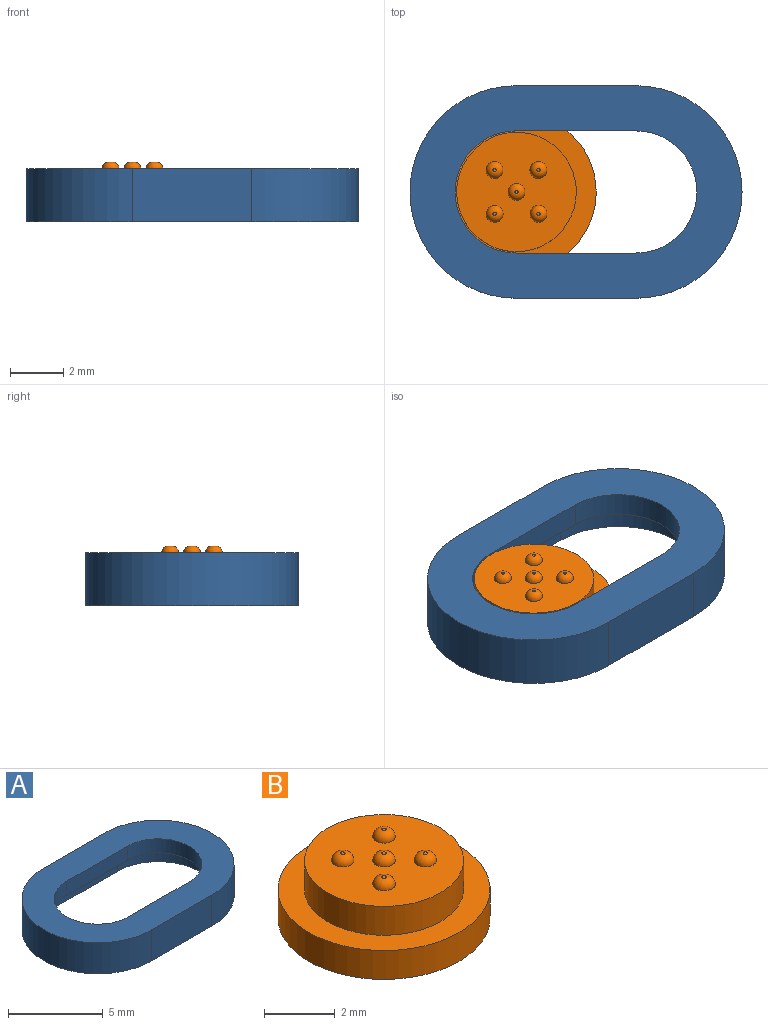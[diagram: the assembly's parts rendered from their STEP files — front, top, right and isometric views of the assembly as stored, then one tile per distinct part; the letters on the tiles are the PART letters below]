
ASSEMBLY  parts=2 mates=1
PART A: 15 faces, bbox 12.5x8x2 mm
  f0: plane 12.5x8mm, normal (0,0,-1), area 29.6mm2, adj f2,f3,f4,f5,f11,f12,f13,f14
  f1: plane 12.5x8mm, normal (0,0,1), area 48.9mm2, adj f2,f3,f4,f5,f6,f7,f8,f9
  f2: plane 4.5x2mm, normal (0,1,0), area 9mm2, adj f0,f1,f3,f5
  f3: cylinder r=4mm len=8mm, axis (0,0,-1), area 25.1mm2, adj f0,f1,f2,f4
  f4: plane 4.5x2mm, normal (0,-1,0), area 9mm2, adj f0,f1,f3,f5
  f5: cylinder r=4mm len=8mm, axis (0,0,-1), area 25.1mm2, adj f0,f1,f2,f4
  f6: plane 4.5x0.9mm, normal (0,-1,0), area 4mm2, adj f1,f7,f9,f10
  f7: cylinder r=2.3mm len=4.6mm, axis (0,0,-1), area 6.5mm2, adj f1,f6,f8,f10
  f8: plane 4.5x0.9mm, normal (0,1,0), area 4mm2, adj f1,f7,f9,f10
  f9: cylinder r=2.3mm len=4.6mm, axis (0,0,-1), area 6.5mm2, adj f1,f6,f8,f10
  f10: plane 10.6x6.1mm, normal (0,0,-1), area 19.4mm2, adj f6,f7,f8,f9,f11,f12,f13,f14
  f11: plane 4.5x1.1mm, normal (0,-1,0), area 5mm2, adj f0,f10,f12,f14
  f12: cylinder r=3.05mm len=6.1mm, axis (0,0,-1), area 10.5mm2, adj f0,f10,f11,f13
  f13: plane 4.5x1.1mm, normal (0,1,0), area 5mm2, adj f0,f10,f12,f14
  f14: cylinder r=3.05mm len=6.1mm, axis (0,0,-1), area 10.5mm2, adj f0,f10,f11,f13
PART B: 15 faces, bbox 6x6x2.3 mm
  f0: cylinder r=3mm len=6mm, axis (0,0,-1), area 18.8mm2, adj f1,f2
  f1: plane 6x6mm, normal (0,0,1), area 12.4mm2, adj f0,f3
  f2: plane 6x6mm, normal (0,0,-1), area 28.3mm2, adj f0
  f3: cylinder r=2.25mm len=4.5mm, axis (0,0,-1), area 14.1mm2, adj f1,f4
  f4: plane 4.5x4.5mm, normal (0,0,1), area 14.3mm2, adj f3,f10,f11,f12,f13,f14
  f5: plane 0.13x0.13mm, normal (0,0,1), area 0mm2, adj f14
  f6: plane 0.13x0.13mm, normal (0,0,1), area 0mm2, adj f13
  f7: plane 0.13x0.13mm, normal (0,0,1), area 0mm2, adj f12
  f8: plane 0.13x0.13mm, normal (0,0,1), area 0mm2, adj f11
  f9: plane 0.13x0.13mm, normal (0,0,1), area 0mm2, adj f10
  f10: torus R=0.06mm, axis (0,0,1), area 0.6mm2, adj f4,f9
  f11: torus R=0.06mm, axis (0,0,1), area 0.6mm2, adj f4,f8
  f12: torus R=0.06mm, axis (0,0,1), area 0.6mm2, adj f4,f7
  f13: torus R=0.06mm, axis (0,0,1), area 0.6mm2, adj f4,f6
  f14: torus R=0.06mm, axis (0,0,1), area 0.6mm2, adj f4,f5
PLACE A t=(0,0.02,-0.96)mm fixed
PLACE B rot(axis=(0,0,1),90.1deg) t=(0.01,0.02,-0.96)mm
MATE pin_slot B.f3 <-> A.f1  axis (0,0,1) through (0.01,0.02,1.04)mm
